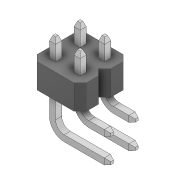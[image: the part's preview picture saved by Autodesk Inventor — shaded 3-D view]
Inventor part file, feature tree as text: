
AUTODESK INVENTOR PART (.ipt)
format: ipt  version: 2020 (Build 240168000, 168)  size: 224,768 bytes
history: native  units: mm
features: chamfer x5, other x3, projected_geometry x3, extrude x2, sketch x2, pattern_linear x1
ambient origin geometry x8: Origin, YZ Plane, XZ Plane, XY Plane, X Axis, Y Axis, Z Axis, Center Point
bodies: Body1 (feature_tree)
feature tree (16):
  other  "솔리드1"
  extrude  "돌출1"  Depth=0.5mm TaperAngle=0.0deg
  other  "작업 평면1"
  extrude  "돌출2"  Depth=1.2mm
  chamfer  "모따기7"  Distance=0.5mm
  chamfer  "모따기8"  Distance=1.2mm
  chamfer  "모따기9"  Distance=0.5mm
  chamfer  "모따기10"  [1 undecoded]
  chamfer  "모따기11"  Distance=0.75mm
  pattern_linear  "직사각형 패턴1"  Spacing1=2.0mm  [1 undecoded]
  sketch  "스케치1"
  sketch  "스케치2"
  projected_geometry  "투영된 루프1"
  projected_geometry  "투영된 루프2"
  projected_geometry  "투영된 루프3"
  other  "작업 평면2"
note: 2 required parameter values undecoded (feature->parameter linkage not recoverable at this tier; creation-order binding heuristic only, values carry confidence <= 0.55)
